# Revit family: VentAxia_NonResidentialVentilation_SentinelApex_HR21
name_source: partatom
category: Mechanical Equipment
units: mm (PartAtom-declared; Revit-internal decimal feet)

## family parameters
Classification = None
Cut with Voids When Loaded = No
Host = Face
OmniClass Number = 23.75.35.21.17
OmniClass Title = Industrial Ventilating Equipment
Part Type = Normal
Room Calculation Point = No
Round Connector Dimension = Use Diameter
Shared = No

## types (1)
- Sentinel Apex - HR21
    A = 2965 mm  [stored 9.72769 ft]
    Assembly Code = D3060400
    AssetType = Fixed
    B = 1319 mm  [stored 4.32743 ft]
    BIMObjectName = VentAxia_NonResidentialVentilation_SentinelApex_HR21
    Black = Plastic, Opaque Black, Vent-Axia
    C = 620 mm  [stored 2.03412 ft]
    ClassificationName = Uniclass2015
    ClassificationValue = Pr_30_59_57_58
    Color = Light Grey
    Cost = 0 $
    Default Elevation = 0 mm  [stored 0 ft]
    Description = Non-Residential Ventilation Sentinel Apex - HR21
    DocumentationCertificates = https://www.bimstore.co
    DocumentationInstallationGuide = https://www.bimstore.co
    DocumentationLiterature = https://www.bimstore.co
    DocumentationMaintenance = https://www.bimstore.co
    DocumentationTechnical = https://www.bimstore.co
    DurationUnit = Years
    E = 88 mm  [stored 0.288714 ft]
    ExpectedLife = 0
    G = 500 mm  [stored 1.64042 ft]
    H = 400 mm  [stored 1.31234 ft]
    I = 1446 mm  [stored 4.74409 ft]
    IfcExportAs = IfcAirTerminal
    IfcExportType = IfcAirTerminalTypeEnum.DIFFUSER
    J = 1359 mm  [stored 4.45866 ft]
    Keynote = U
    LightGrey = Metal, Paint Finish, Light Grey, Vent-Axia
    Manufacturer = Vent-Axia Limited
    ManufacturerName = Vent-Axia Limited
    Model = Non-Residential Ventilation Sentinel Apex - HR21
    ModelNumber = Sentinel Apex - HR21
    ModelReference = Non-Residential Ventilation
    NBSDescription = Overhead ventilators
    NBSObjectName = Vent-Axia - Overhead ventilators
    NBSReference = 45-25-97/360
    NominalDepth = 1446 mm  [stored 4.74409 ft]
    NominalHeight = 620 mm  [stored 2.03412 ft]
    NominalLength = 2965 mm  [stored 9.72769 ft]
    ProductionYear = 2023
    Red = Plastic, Opaque Red, Vent-Axia
    Type Comments = Non-Residential Ventilation Sentinel Apex - HR21
    TypeName = Non-Residential Ventilation Sentinel Apex - HR21
    URL = https://www.vent-axia.com
    WarrantyDurationLabor = 0
    WarrantyDurationParts = 0
    WarrantyDurationUnit = Years
    White = Plastic, Opaque White, Vent-Axia
    Yellow = Plastic, Opaque Yellow, Vent-Axia
    _BSBibleVersion = 17
    _BimSpecGuid = 0
    _CurrentRevision = 1
    _DistributedBy = https://www.bimstore.co
    _ObjectUserGuide = https://www.bimstore.co

note: [stored X ft] marks values corroborated as IEEE doubles in the binary element streams (Revit-internal decimal feet)

## geometry (parser evidence)
native form markers: Sweep x3
no freeform markers — native parametric forms only
